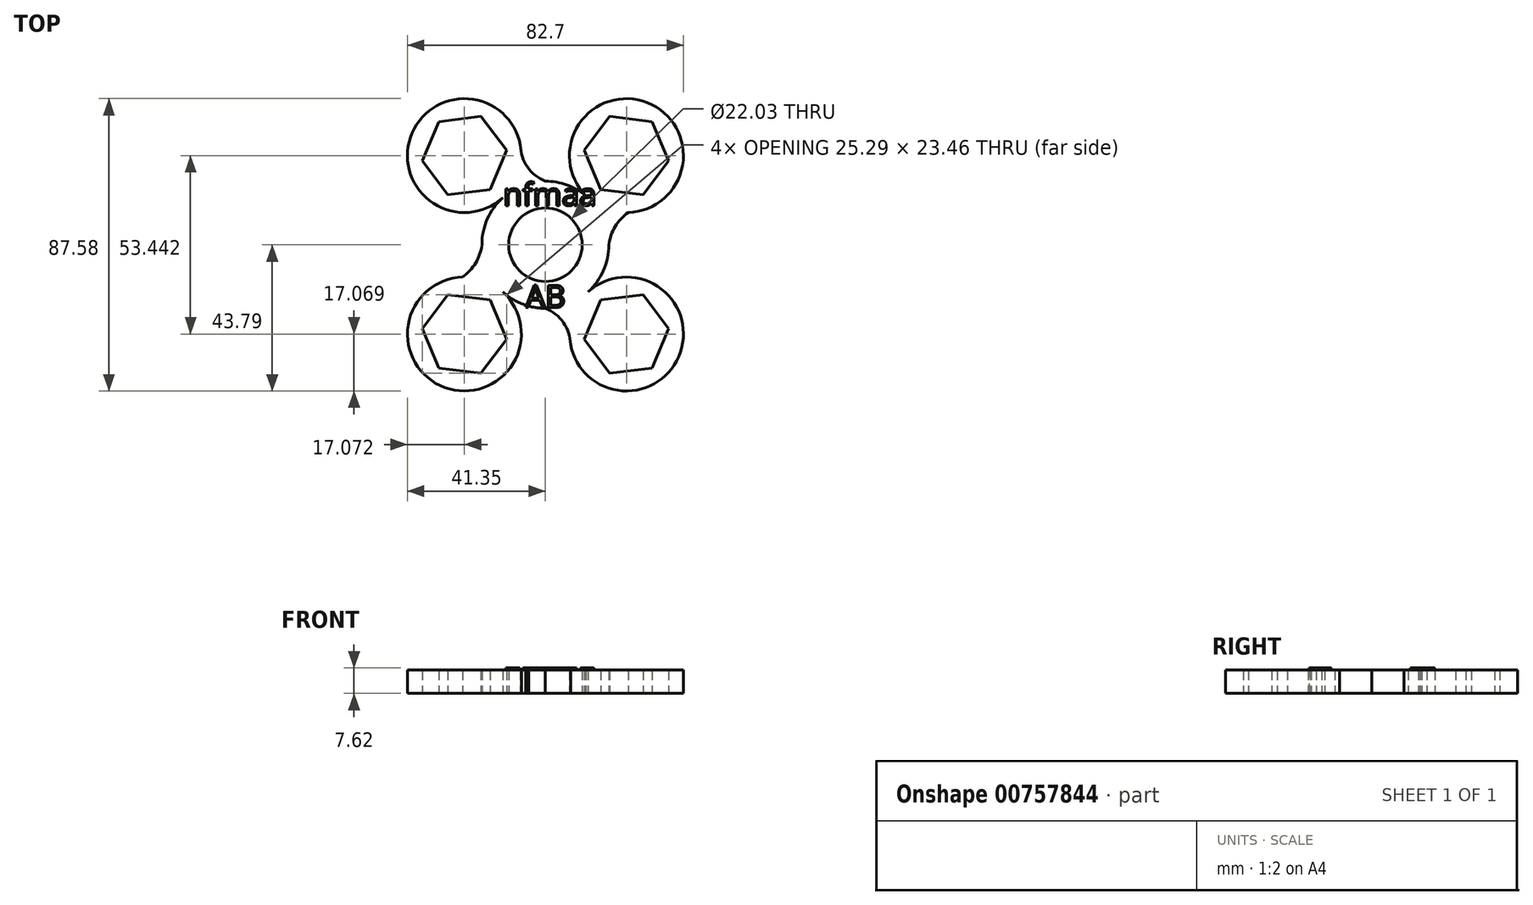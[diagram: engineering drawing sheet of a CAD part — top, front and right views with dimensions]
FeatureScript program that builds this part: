
annotation { "Feature Type Name" : "Feature", "Feature Type Description" : "" }
export const myFeature = defineFeature(function(context is Context, id is Id, definition is map)
    precondition{}
    {
        {
            var Q0;
            Q0=qCreatedBy(makeId("Top.planeOp"),FACE);
            var sketch = newSketch(context, id + "F0", { "sketchPlane" : qUnion([Q0])});
            skCircle(sketch, "E0", {"center": v(0, 0) * mm, "radius": 11.01 * mm});
            skCircle(sketch, "E1", {"center": v(0, 0) * mm, "radius": 19.03 * mm});
            skPoint(sketch, "E2", {"position": v(-24.28, 26.72) * mm});
            skLineSegment(sketch, "E3.0", {"start": v(-11.63, 28.28) * mm, "end": v(-16.6, 16.55) * mm});
            skLineSegment(sketch, "E3.1", {"start": v(-16.6, 16.55) * mm, "end": v(-29.25, 15) * mm});
            skLineSegment(sketch, "E3.2", {"start": v(-29.25, 15) * mm, "end": v(-36.92, 25.16) * mm});
            skLineSegment(sketch, "E3.3", {"start": v(-36.92, 25.16) * mm, "end": v(-31.95, 36.9) * mm});
            skLineSegment(sketch, "E3.4", {"start": v(-31.95, 36.9) * mm, "end": v(-19.3, 38.45) * mm});
            skLineSegment(sketch, "E3.5", {"start": v(-19.3, 38.45) * mm, "end": v(-11.63, 28.28) * mm});
            skPoint(sketch, "E3.0.midPoint", {"position": v(-14.12, 22.41) * mm});
            skCircle(sketch, "E4", {"center": v(-24.28, 26.72) * mm, "radius": 17.07 * mm});
            skLineSegment(sketch, "E5.MirrorCS", {"start": v(11.63, 28.28) * mm, "end": v(16.6, 16.55) * mm});
            skLineSegment(sketch, "E6.MirrorCS", {"start": v(29.25, 15) * mm, "end": v(36.92, 25.16) * mm});
            skLineSegment(sketch, "E7.MirrorCS", {"start": v(36.92, 25.16) * mm, "end": v(31.95, 36.9) * mm});
            skLineSegment(sketch, "E8.MirrorCS", {"start": v(31.95, 36.9) * mm, "end": v(19.3, 38.45) * mm});
            skLineSegment(sketch, "E9.MirrorCS", {"start": v(19.3, 38.45) * mm, "end": v(11.63, 28.28) * mm});
            skLineSegment(sketch, "E10.MirrorCS", {"start": v(16.6, 16.55) * mm, "end": v(29.25, 15) * mm});
            skPoint(sketch, "E11.MirrorP", {"position": v(24.28, 26.72) * mm});
            skPoint(sketch, "E12.MirrorP", {"position": v(14.12, 22.41) * mm});
            skCircle(sketch, "E13.MirrorC", {"center": v(24.28, 26.72) * mm, "radius": 17.07 * mm});
            skPoint(sketch, "E14.MirrorP", {"position": v(-24.28, -26.72) * mm});
            skLineSegment(sketch, "E15.MirrorCS", {"start": v(-36.92, -25.16) * mm, "end": v(-31.95, -36.9) * mm});
            skLineSegment(sketch, "E16.MirrorCS", {"start": v(-11.63, -28.28) * mm, "end": v(-16.6, -16.55) * mm});
            skLineSegment(sketch, "E17.MirrorCS", {"start": v(-19.3, -38.45) * mm, "end": v(-11.63, -28.28) * mm});
            skLineSegment(sketch, "E18.MirrorCS", {"start": v(-29.25, -15) * mm, "end": v(-36.92, -25.16) * mm});
            skLineSegment(sketch, "E19.MirrorCS", {"start": v(-16.6, -16.55) * mm, "end": v(-29.25, -15) * mm});
            skLineSegment(sketch, "E20.MirrorCS", {"start": v(-31.95, -36.9) * mm, "end": v(-19.3, -38.45) * mm});
            skPoint(sketch, "E21.MirrorP", {"position": v(-14.12, -22.41) * mm});
            skCircle(sketch, "E22.MirrorC", {"center": v(-24.28, -26.72) * mm, "radius": 17.07 * mm});
            skPoint(sketch, "E23.MirrorP", {"position": v(24.28, -26.72) * mm});
            skLineSegment(sketch, "E24.MirrorCS", {"start": v(11.63, -28.28) * mm, "end": v(16.6, -16.55) * mm});
            skLineSegment(sketch, "E25.MirrorCS", {"start": v(19.3, -38.45) * mm, "end": v(11.63, -28.28) * mm});
            skLineSegment(sketch, "E26.MirrorCS", {"start": v(16.6, -16.55) * mm, "end": v(29.25, -15) * mm});
            skLineSegment(sketch, "E27.MirrorCS", {"start": v(31.95, -36.9) * mm, "end": v(19.3, -38.45) * mm});
            skPoint(sketch, "E28.MirrorP", {"position": v(14.12, -22.41) * mm});
            skLineSegment(sketch, "E29.MirrorCS", {"start": v(36.92, -25.16) * mm, "end": v(31.95, -36.9) * mm});
            skCircle(sketch, "E30.MirrorC", {"center": v(24.28, -26.72) * mm, "radius": 17.07 * mm});
            skLineSegment(sketch, "E31.MirrorCS", {"start": v(29.25, -15) * mm, "end": v(36.92, -25.16) * mm});
            skArc(sketch, "E32", {"start": v(-24.86, -9.66) * mm, "mid": v(-20.91, -5.45) * mm, "end": v(-19.03, 0) * mm});
            skArc(sketch, "E33", {"start": v(-7.5, 29.88) * mm, "mid": v(-5.39, 23.33) * mm, "end": v(0, 19.03) * mm});
            skArc(sketch, "E34.MirrorCS", {"start": v(-24.86, 9.66) * mm, "mid": v(-20.91, 5.45) * mm, "end": v(-19.03, 0) * mm});
            skArc(sketch, "E35.MirrorCS", {"start": v(-7.5, -29.88) * mm, "mid": v(-5.39, -23.33) * mm, "end": v(0, -19.03) * mm});
            skArc(sketch, "E36.MirrorCS", {"start": v(24.86, 9.66) * mm, "mid": v(20.91, 5.45) * mm, "end": v(19.03, 0) * mm});
            skArc(sketch, "E37.MirrorCS", {"start": v(24.86, -9.66) * mm, "mid": v(20.91, -5.45) * mm, "end": v(19.03, 0) * mm});
            skArc(sketch, "E38.MirrorCS", {"start": v(7.5, -29.88) * mm, "mid": v(5.39, -23.33) * mm, "end": v(0, -19.03) * mm});
            skArc(sketch, "E39.MirrorCS", {"start": v(7.5, 29.88) * mm, "mid": v(5.39, 23.33) * mm, "end": v(0, 19.03) * mm});
            skSolve(sketch);
        }
        {
            var Q0;
            Q0=qCreatedBy(makeId("Top.planeOp"),FACE);
            var sketch = newSketch(context, id + "F1", { "sketchPlane" : qUnion([Q0])});
            skText(sketch, "E40", { "text": "nfmaa", "fontName": "OpenSans-Regular.ttf"});
            skText(sketch, "E41", { "text": "AB", "fontName": "OpenSans-Regular.ttf"});
            const initialGuessF1  = {"E40": [-0.01267, 0.01176, 1, 0, 0.00672], "E41": [-0.00595, -0.01878, 1, 0, 0.00672]};
            skSetInitialGuess(sketch, initialGuessF1);
            skSolve(sketch);
        }
        {
            var Q0;
            Q0=makeQuery(id+"F0.imprint","IMPRINT",FACE,{"disambiguationData":[TD([[makeQuery(id+"F0.imprint","IMPRINT",EDGE,{"derivedFrom":sQuery(id+"F0.wireOp",EDGE,"E5.MirrorCS")}),-1.0]])]});
            var Q1;
            Q1=makeQuery(id+"F0.imprint","IMPRINT",FACE,{"disambiguationData":[TD([[makeQuery(id+"F0.imprint","IMPRINT",EDGE,{"derivedFrom":sQuery(id+"F0.wireOp",EDGE,"E3.0")}),1.0]])]});
            var Q2;
            Q2=makeQuery(id+"F0.imprint","IMPRINT",FACE,{"disambiguationData":[TD([[makeQuery(id+"F0.imprint","IMPRINT",EDGE,{"derivedFrom":sQuery(id+"F0.wireOp",EDGE,"E16.MirrorCS")}),-1.0]])]});
            var Q3;
            Q3=makeQuery(id+"F0.imprint","IMPRINT",FACE,{"disambiguationData":[TD([[makeQuery(id+"F0.imprint","IMPRINT",EDGE,{"derivedFrom":sQuery(id+"F0.wireOp",EDGE,"E24.MirrorCS")}),1.0]])]});
            var Q4;
            Q4=makeQuery(id+"F0.imprint","IMPRINT",FACE,{"disambiguationData":[TD([[makeQuery(id+"F0.imprint","IMPRINT",EDGE,{"derivedFrom":sQuery(id+"F0.wireOp",EDGE,"E0")}),-1.0]])]});
            var Q5;
            {var subQ0=sQuery(id+"F0.wireOp",EDGE,"E32");Q5=makeQuery(id+"F0.imprint","IMPRINT",FACE,{"disambiguationData":[TD([[makeQuery(id+"F0.imprint","IMPRINT",EDGE,{"derivedFrom":subQ0}),-1.0]])]});}
            var Q6;
            {var subQ0=sQuery(id+"F0.wireOp",EDGE,"E35.MirrorCS");var subQ3=sQuery(id+"F0.wireOp",EDGE,"E22.MirrorC");var subQ5=makeQuery(id+"F0.imprint","INTERSECT",VERTEX,{"disambiguationData":[OD(1.0)],"derivedFrom":[subQ3,subQ0]});Q6=makeQuery(id+"F0.imprint","IMPRINT",FACE,{"disambiguationData":[TD([[makeQuery(id+"F0.imprint","IMPRINT",EDGE,{"disambiguationData":[TD([[subQ5,1.0]])],"derivedFrom":subQ3}),1.0]])]});}
            var Q7;
            {var subQ0=sQuery(id+"F0.wireOp",EDGE,"E38.MirrorCS");var subQ3=sQuery(id+"F0.wireOp",EDGE,"E30.MirrorC");var subQ5=makeQuery(id+"F0.imprint","INTERSECT",VERTEX,{"disambiguationData":[OD(1.0)],"derivedFrom":[subQ3,subQ0]});Q7=makeQuery(id+"F0.imprint","IMPRINT",FACE,{"disambiguationData":[TD([[makeQuery(id+"F0.imprint","IMPRINT",EDGE,{"disambiguationData":[TD([[subQ5,1.0]])],"derivedFrom":subQ3}),-1.0]])]});}
            var Q8;
            {var subQ0=sQuery(id+"F0.wireOp",EDGE,"E37.MirrorCS");Q8=makeQuery(id+"F0.imprint","IMPRINT",FACE,{"disambiguationData":[TD([[makeQuery(id+"F0.imprint","IMPRINT",EDGE,{"derivedFrom":subQ0}),1.0]])]});}
            var Q9;
            {var subQ0=sQuery(id+"F0.wireOp",EDGE,"E36.MirrorCS");Q9=makeQuery(id+"F0.imprint","IMPRINT",FACE,{"disambiguationData":[TD([[makeQuery(id+"F0.imprint","IMPRINT",EDGE,{"derivedFrom":subQ0}),-1.0]])]});}
            var Q10;
            {var subQ0=sQuery(id+"F0.wireOp",EDGE,"E39.MirrorCS");var subQ3=sQuery(id+"F0.wireOp",EDGE,"E13.MirrorC");var subQ5=makeQuery(id+"F0.imprint","INTERSECT",VERTEX,{"disambiguationData":[OD(1.0)],"derivedFrom":[subQ3,subQ0]});Q10=makeQuery(id+"F0.imprint","IMPRINT",FACE,{"disambiguationData":[TD([[makeQuery(id+"F0.imprint","IMPRINT",EDGE,{"disambiguationData":[TD([[subQ5,1.0]])],"derivedFrom":subQ3}),1.0]])]});}
            var Q11;
            {var subQ0=sQuery(id+"F0.wireOp",EDGE,"E33");var subQ3=sQuery(id+"F0.wireOp",EDGE,"E4");var subQ5=makeQuery(id+"F0.imprint","INTERSECT",VERTEX,{"disambiguationData":[OD(1.0)],"derivedFrom":[subQ3,subQ0]});Q11=makeQuery(id+"F0.imprint","IMPRINT",FACE,{"disambiguationData":[TD([[makeQuery(id+"F0.imprint","IMPRINT",EDGE,{"disambiguationData":[TD([[subQ5,1.0]])],"derivedFrom":subQ3}),-1.0]])]});}
            var Q12;
            {var subQ0=sQuery(id+"F0.wireOp",EDGE,"E34.MirrorCS");Q12=makeQuery(id+"F0.imprint","IMPRINT",FACE,{"disambiguationData":[TD([[makeQuery(id+"F0.imprint","IMPRINT",EDGE,{"derivedFrom":subQ0}),1.0]])]});}
            extrude(context, id + "F2", {"entities" : qUnion([Q0, Q1, Q2, Q3, Q4, Q5, Q6, Q7, Q8, Q9, Q10, Q11, Q12]), "depth" : 7 * mm, "offsetDistance" : 25.4 * mm});
        }
        {
            var Q0;
            Q0 = qSketchRegion(id + "F1", true);
            extrude(context, id + "F3", {"entities" : qUnion([Q0]), "operationType" : NewBodyOperationType.ADD, "depth" : 7.62 * mm, "offsetDistance" : 25.4 * mm});
        }
    });
